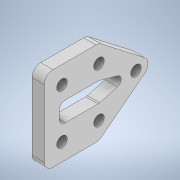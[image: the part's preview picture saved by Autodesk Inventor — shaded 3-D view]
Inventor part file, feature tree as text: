
AUTODESK INVENTOR PART (.ipt)
format: ipt  version: 2021 (Build 250183000, 183)  size: 150,528 bytes
history: native  units: mm
features: extrude x2, fillet x2, sketch x2
ambient origin geometry x8: Origin, YZ Plane, XZ Plane, XY Plane, X Axis, Y Axis, Z Axis, Center Point
bodies: Solid1 (feature_tree)
feature tree (6):
  extrude  "Extrusion1"  Depth=8.5mm
  fillet  "Fillet1"  Radius=14.25mm
  extrude  "Extrusion2"  Depth=5.0mm
  fillet  "Fillet2"  Radius=10.0mm
  sketch  "Sketch1"  dims[d6=8.5mm d9=8.5mm d10=14.25mm]
  sketch  "Sketch2"  dims[d11=14.25mm d13=14.25mm d14=10.0mm d15=0.0mm d16=7.0mm d23=10.0mm d24=0.0mm d25=5.0mm]
